# Revit family: xx
name_source: partatom
category: Mechanical Equipment
revit_build: Autodesk Revit MEP 2015 (Build: 20150303_1515(x64)
units: mm (PartAtom-declared; Revit-internal decimal feet)

## types (1)
- Boiling, chilled and filtered- 2924UK Compact Base unit
    6 Monthly Maintenance (or SFG20 Codes) = 6 monthly filter change recommended
    BMS Links = No
    Backflow Prevention Valve = Not Included
    Base Unit Finish = white Enamel
    Button Interface = No
    Cable Length and size (If Fitted) = 3.0m
    Capacity = 16.7 Litres
    Classic HydroTap Clearance ( if fitted to font + ext ) = 222mm
    Cost = 0 $
    Environmental Product Declaration = http://www.environdec.com
    Features = Touch Screen Features control
    Insulation Material = High Density PE
    Internal Filter (if fitted) = Yes
    Location of Manufacturer = Australia
    Mains Pressure Limiting Valve = not included
    Mains Water Connection = 1/2" BSP
    Mains Water Pressure _ Maximum = 0.7 MPa (7 bar)
    Mains Water Pressure _ Minimum = 0.17 MPa (1.7 bar)
    Manufacturer = Zip Industries(UK) Ltd
    Maximum Stored Water Temperature = 98°C
    Model = BC(C)-2924UK
    Net Weight = 22.0 kg
    Overall Height = 335mm
    Overall Length = 470mm
    Overall Width = 280mm
    Power Rating = 2.05A
    Power Supply (Voltage) = 230V (50~60Hz)
    Product Range = Floor Mounted
    Programmable Function Parameters = Yes
    Programmable Safety Features = Yes
    Shape = Rectangular
    Supply Phase = 1 Phase
    Tank Construction Material = Stainless steel
    Type = Vented / Non-vented (depending on pipe work arrangement)
    Type Comments = Water Boiler and Chiller (Potable)
    Type Image = <None>
    URL = www.zipindustries.co.uk
    Unit Access Clearance Left = 50mm
    Unit Access Clearance Top = 200mm
    Unit Access Clearance right = 50mm
    WRAS Approved = Yes
    Warranty ID = 2years
    Wireless (WIFI) = Yes

## geometry (parser evidence)
native form markers: Blend x8, Sweep x2
no freeform markers — native parametric forms only
